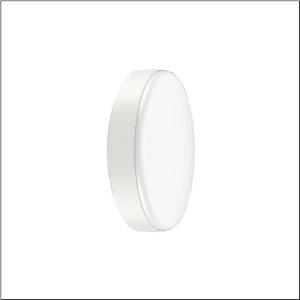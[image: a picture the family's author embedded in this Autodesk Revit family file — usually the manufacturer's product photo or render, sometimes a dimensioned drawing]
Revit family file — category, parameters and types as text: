
# Revit family: round_31_51wc10db34as
name_source: partatom
category: Lighting Fixtures
units: mm (PartAtom-declared; Revit-internal decimal feet)

## family parameters
Cut with Voids When Loaded = No
Host = Face
Light Source = No
Part Type = Normal
Room Calculation Point = No
Round Connector Dimension = Use Diameter
Shared = No

## types (1)
- Round 31 (1 x LED, 4250 lm, 35.4 W, 3000K)
    Apparent Load = 35 VA
    CIE Flux Codes = 44 75 94 94 100
    Color Rendering = 80
    Color Temperature = 3000K
    Default Elevation = 1800 mm
    Description = Round 31, wall and ceiling luminaire, primary optical cover: cover, of PC, opal, light emission: direct distribution, primary light characteristic: symmetric, installation type: surface-mounted, LED, rated luminous flux: 4.250lm, luminous efficacy: 120lm/W, light colour: 830, colour temperature: 3000K, control gear: DALI 2, with terminal, 5-pole, max. 2.5mm², mains connection: 220..240V, AC, 50/60Hz, rated input power: 35.5W, luminaire housing, of PC, traffic white (RAL 9016), diameter: 480mm, brightness and presence sensor, HF sensor, protection rating (complete): IP65, insulation class (complete): insulation class II (safety insulation), certification: CE, impact resistance: IK10, permissible operating ambient temperature: -20..+40°C, permissible storage temperature: -20..+60°C, packaging unit: 1 piece
    Height = 97 mm
    Lamp = 1 x LED
    Lamp Light Flux = 4250 lm
    Lamp Power = 35.4 W
    Lamp count = 1
    Length = 480 mm
    Luminous efficacy = 120 lm/W
    Manufacturer = Siteco
    ModVariant = No
    Model = 51WC10DB34AS
    Mounting Place = Wall
    Mounting Type = Surface mounted
    Number of Poles = 1
    OnlyDefault = Yes
    Power Factor = 1
    Product Name = Round 31
    Product group = wall and ceiling luminaire | wall mounted
    ProductGroupID = 2001
    Protection Class = Protection class II
    Protection Degree = IP 65
    RLX_Detail_Level = 1
    RLX_Emergency_Light_Flux = 0 lm
    RLX_Emergency_Type = 0
    RLX_Emergency_Type_DB = No
    RlxData = <blob elided: 40893 chars, md5=a47d0047>
    Socket = socket
    Standby Power = 0 W
    System Light Flux = 4250 lm
    System Power = 35 W
    Type Comments = Product without accessories
    Type Image = l_1007188.jpg
    URL = http://relux.com
    VarID = ---
    Voltage = 0 V
    Weight = 0.00 kg
    Width = 0 mm  [stored 0 ft]

note: [stored X ft] marks values corroborated as IEEE doubles in the binary element streams (Revit-internal decimal feet)

## geometry (parser evidence)
native form markers: Blend x4, Sweep x13
no freeform markers — native parametric forms only
